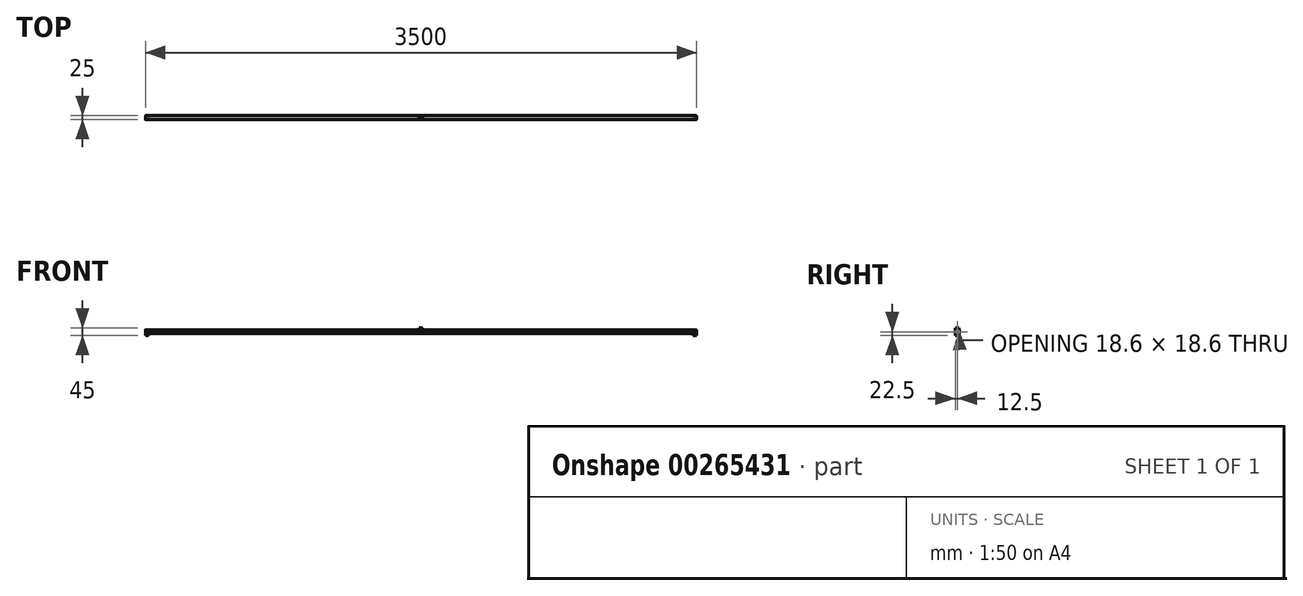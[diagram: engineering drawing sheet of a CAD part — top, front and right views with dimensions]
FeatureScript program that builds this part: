
annotation { "Feature Type Name" : "Feature", "Feature Type Description" : "" }
export const myFeature = defineFeature(function(context is Context, id is Id, definition is map)
    precondition{}
    {
        {
            var Q0;
            Q0=qCreatedBy(makeId("Right.planeOp"),FACE);
            var sketch = newSketch(context, id + "F0", { "sketchPlane" : qUnion([Q0])});
            skLineSegment(sketch, "E0.bottom", {"start": v(10.5, 12.5) * mm, "end": v(-10.5, 12.5) * mm});
            skLineSegment(sketch, "E0.top", {"start": v(10.5, -12.5) * mm, "end": v(-10.5, -12.5) * mm});
            skLineSegment(sketch, "E0.left", {"start": v(12.5, 10.5) * mm, "end": v(12.5, -10.5) * mm});
            skLineSegment(sketch, "E0.right", {"start": v(-12.5, 10.5) * mm, "end": v(-12.5, -10.5) * mm});
            skPoint(sketch, "E0.middle", {"position": v(0, 0) * mm});
            skLineSegment(sketch, "E1.bottom", {"start": v(7.3, 9.3) * mm, "end": v(-7.3, 9.3) * mm});
            skLineSegment(sketch, "E1.top", {"start": v(7.3, -9.3) * mm, "end": v(-7.3, -9.3) * mm});
            skLineSegment(sketch, "E1.left", {"start": v(9.3, 7.3) * mm, "end": v(9.3, -7.3) * mm});
            skLineSegment(sketch, "E1.right", {"start": v(-9.3, 7.3) * mm, "end": v(-9.3, -7.3) * mm});
            skPoint(sketch, "E2.visualSharp", {"position": v(-12.5, 12.5) * mm});
            skArc(sketch, "E2.filletArc", {"start": v(-10.5, 12.5) * mm, "mid": v(-11.91, 11.91) * mm, "end": v(-12.5, 10.5) * mm});
            skPoint(sketch, "E3.visualSharp", {"position": v(12.5, 12.5) * mm});
            skArc(sketch, "E3.filletArc", {"start": v(12.5, 10.5) * mm, "mid": v(11.91, 11.91) * mm, "end": v(10.5, 12.5) * mm});
            skPoint(sketch, "E4.visualSharp", {"position": v(9.3, 9.3) * mm});
            skArc(sketch, "E4.filletArc", {"start": v(9.3, 7.3) * mm, "mid": v(8.71, 8.71) * mm, "end": v(7.3, 9.3) * mm});
            skPoint(sketch, "E5.visualSharp", {"position": v(12.5, -12.5) * mm});
            skArc(sketch, "E5.filletArc", {"start": v(10.5, -12.5) * mm, "mid": v(11.91, -11.91) * mm, "end": v(12.5, -10.5) * mm});
            skPoint(sketch, "E6.visualSharp", {"position": v(9.3, -9.3) * mm});
            skArc(sketch, "E6.filletArc", {"start": v(7.3, -9.3) * mm, "mid": v(8.71, -8.71) * mm, "end": v(9.3, -7.3) * mm});
            skPoint(sketch, "E7.visualSharp", {"position": v(-9.3, -9.3) * mm});
            skArc(sketch, "E7.filletArc", {"start": v(-9.3, -7.3) * mm, "mid": v(-8.71, -8.71) * mm, "end": v(-7.3, -9.3) * mm});
            skPoint(sketch, "E8.visualSharp", {"position": v(-12.5, -12.5) * mm});
            skArc(sketch, "E8.filletArc", {"start": v(-12.5, -10.5) * mm, "mid": v(-11.91, -11.91) * mm, "end": v(-10.5, -12.5) * mm});
            skPoint(sketch, "E9.visualSharp", {"position": v(-9.3, 9.3) * mm});
            skArc(sketch, "E9.filletArc", {"start": v(-7.3, 9.3) * mm, "mid": v(-8.71, 8.71) * mm, "end": v(-9.3, 7.3) * mm});
            skSolve(sketch);
        }
        {
            var Q0;
            Q0=makeQuery(id+"F0.imprint","IMPRINT",FACE,{"disambiguationData":[TD([[makeQuery(id+"F0.imprint","IMPRINT",EDGE,{"derivedFrom":sQuery(id+"F0.wireOp",EDGE,"E0.bottom")}),1.0]])]});
            extrude(context, id + "F1", {"entities" : qUnion([Q0]), "endBound" : BoundingType.SYMMETRIC, "depth" : 3500 * mm});
        }
        {
            var Q0;
            Q0=makeQuery(id+"F1.opExtrude","SWEPT_FACE",FACE,{"disambiguationData":[OSD([sQuery(id+"F0.wireOp",EDGE,"E0.bottom")])]});
            var sketch = newSketch(context, id + "F2", { "sketchPlane" : qUnion([Q0])});
            skLineSegment(sketch, "E10.bottom", {"start": v(10.54, 10.5) * mm, "end": v(-10.54, 10.5) * mm});
            skLineSegment(sketch, "E10.top", {"start": v(10.54, -10.5) * mm, "end": v(-10.54, -10.5) * mm});
            skLineSegment(sketch, "E10.left", {"start": v(10.54, 10.5) * mm, "end": v(10.54, -10.5) * mm});
            skLineSegment(sketch, "E10.right", {"start": v(-10.54, 10.5) * mm, "end": v(-10.54, -10.5) * mm});
            skPoint(sketch, "E10.middle", {"position": v(0, 0) * mm});
            skSolve(sketch);
        }
        {
            var Q0;
            Q0=makeQuery(id+"F2.imprint","IMPRINT",FACE,{"disambiguationData":[TD([[makeQuery(id+"F2.imprint","IMPRINT",EDGE,{"derivedFrom":sQuery(id+"F2.wireOp",EDGE,"E10.bottom")}),1.0]])]});
            extrude(context, id + "F3", {"entities" : qUnion([Q0]), "operationType" : NewBodyOperationType.ADD, "depth" : 10 * mm});
        }
        {
            var Q0;
            Q0=makeQuery(id+"F1.opExtrude","SWEPT_FACE",FACE,{"disambiguationData":[OSD([sQuery(id+"F0.wireOp",EDGE,"E0.top")])]});
            var sketch = newSketch(context, id + "F4", { "sketchPlane" : qUnion([Q0])});
            skLineSegment(sketch, "E11.bottom", {"start": v(-1750, -10.5) * mm, "end": v(-1729.1, -10.5) * mm});
            skLineSegment(sketch, "E11.top", {"start": v(-1750, 10.5) * mm, "end": v(-1729.1, 10.5) * mm});
            skLineSegment(sketch, "E11.left", {"start": v(-1750, -10.5) * mm, "end": v(-1750, 10.5) * mm});
            skLineSegment(sketch, "E11.right", {"start": v(-1729.1, -10.5) * mm, "end": v(-1729.1, 10.5) * mm});
            skLineSegment(sketch, "E12.bottom", {"start": v(1750, -10.5) * mm, "end": v(1729.14, -10.5) * mm});
            skLineSegment(sketch, "E12.top", {"start": v(1750, 10.5) * mm, "end": v(1729.14, 10.5) * mm});
            skLineSegment(sketch, "E12.left", {"start": v(1750, -10.5) * mm, "end": v(1750, 10.5) * mm});
            skLineSegment(sketch, "E12.right", {"start": v(1729.14, -10.5) * mm, "end": v(1729.14, 10.5) * mm});
            skSolve(sketch);
        }
        {
            var Q0;
            Q0=makeQuery(id+"F4.imprint","IMPRINT",FACE,{"disambiguationData":[TD([[makeQuery(id+"F4.imprint","IMPRINT",EDGE,{"derivedFrom":sQuery(id+"F4.wireOp",EDGE,"E11.bottom")}),-1.0]])]});
            var Q1;
            Q1=makeQuery(id+"F4.imprint","IMPRINT",FACE,{"disambiguationData":[TD([[makeQuery(id+"F4.imprint","IMPRINT",EDGE,{"derivedFrom":sQuery(id+"F4.wireOp",EDGE,"E12.bottom")}),-1.0]])]});
            extrude(context, id + "F5", {"entities" : qUnion([Q0, Q1]), "operationType" : NewBodyOperationType.ADD, "depth" : 10 * mm});
        }
    });
